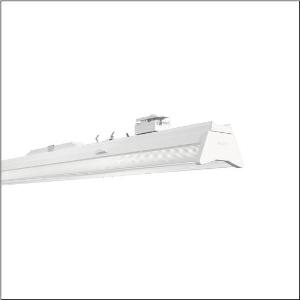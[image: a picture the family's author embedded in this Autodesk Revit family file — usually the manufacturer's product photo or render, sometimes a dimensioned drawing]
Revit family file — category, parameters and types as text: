
# Revit family: licross_11_performance_ho_51td16cn4exm
name_source: partatom
category: Lighting Fixtures
units: mm (PartAtom-declared; Revit-internal decimal feet)

## family parameters
Cut with Voids When Loaded = No
Host = Face
Light Source = No
Part Type = Normal
Room Calculation Point = No
Round Connector Dimension = Use Diameter
Shared = No

## types (1)
- --- (1 x LED, 14420 lm, 77.6 W, 4000K)
    Apparent Load = 78 VA
    CIE Flux Codes = 63 87 95 78 100
    Color Rendering = 80
    Color Temperature = 4000K
    Default Elevation = 1800 mm
    Description = Licross 11 Performance HO, luminaire insert, of sheet steel, galvanised, coil coated, white, length: 1.500mm, width: 120mm, height: 123mm, LED rated luminous flux: 14.420lm, light colour: 840, SDCM (Standard Deviation of Colour Matching)MacAdam ≤ 2 SDCM (initial), control gear: ON/OFF Multilumen, CLOi, with plug, 3-pole, with phase selection, mains connection: 220..240V, AC, 50/60Hz, start of lifetime: 78W, end of service life: 87W, internal wiring halogen-free, primary light control with lens, of plastic, primary optical cover: cover, of PMMA, light emission: direct/indirect distribution, primary light characteristic: symmetric, protection rating (complete): IP54, insulation class (complete): insulation class I (protective earthing), certification: CE, ENEC, VDE, UKCA, protection symbol: D if used in an environment with non-conductive dust loads with corresponding accessories, impact resistance: IK06, permissible ambient temperature for indoor applications: -35..+35°C, corresponds to IFS (International Featured Standards) requirements for safety and quality in the food industry, reducing of maximum allowable ambient temperature of 5°C with ceiling mounting, LABS conformity tested according to VDMA 24364:2018-05, The light source and the operating device comply with the requirements of the Ecodesign Regulation (EU) 2019/2020 and are replaceable in accordance with this regulation, packaging unit: 1 piece
    Height = 114 mm
    Lamp = 1 x LED
    Lamp Light Flux = 14420 lm
    Lamp Power = 77.6 W
    Lamp count = 1
    Length = 1500 mm
    Luminous efficacy = 186 lm/W
    Manufacturer = Siteco
    ModVariant = No
    Model = 51TD16CN4EXM
    Mounting Place = Ceiling
    Mounting Type = Pendant
    Number of Poles = 1
    OnlyDefault = Yes
    Power Factor = 1
    Product Name = Licross 11 Performance HO
    Product group = luminaire insert | ceiling pendant
    ProductGroupID = 901
    Protection Class = Protection class I
    Protection Degree = IP 54
    RLX_Detail_Level = 1
    RLX_Emergency_Light_Flux = 0 lm
    RLX_Emergency_Type = 0
    RLX_Emergency_Type_DB = No
    RlxData = <blob elided: 32173 chars, md5=e42cb526>
    Socket = socket
    Standby Power = 0 W
    System Light Flux = 14420 lm
    System Power = 78 W
    Type Comments = factory setting: luminous flux: 100 % | (A | C | E) | 181 mA
    Type Image = l_1256138.jpg
    URL = http://relux.com
    VarID = @adj_001331
    Voltage = 0 V
    Weight = 0.00 kg
    Width = 120 mm

## geometry (parser evidence)
native form markers: Blend x4, Sweep x12
no freeform markers — native parametric forms only
